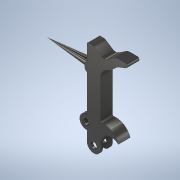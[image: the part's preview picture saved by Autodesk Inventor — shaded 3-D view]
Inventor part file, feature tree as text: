
AUTODESK INVENTOR PART (.ipt)
format: ipt  version: 2021 (Build 250183000, 183)  size: 390,144 bytes
history: native  units: in
note: dims shown in document units (in); Inventor stores cm internally (conversion verified against a paired STEP export)
features: extrude x8, sketch x8, plane x6, fillet x4, projected_geometry x2, revolve x1
ambient origin geometry x8: Origin, YZ Plane, XZ Plane, XY Plane, X Axis, Y Axis, Z Axis, Center Point
bodies: Solid1 (feature_tree)
feature tree (29):
  extrude  "Extrusion1"  Depth=0.9843in
  extrude  "Extrusion2"  Depth=0.0787in
  plane  "Work Plane1"
  extrude  "Extrusion3"  Depth=0.1575in TaperAngle=0.0deg
  plane  "Work Plane2"
  extrude  "Extrusion4"  Depth=0.0276in
  plane  "Work Plane3"
  fillet  "Fillet4"  Radius=0.22in
  plane  "Work Plane6"
  extrude  "Extrusion8"  Depth=0.0504in
  fillet  "Fillet8"  Radius=0.22in
  fillet  "Fillet9"  Radius=0.0157in
  plane  "Work Plane7"
  sketch  "Sketch10"  dims[d147=0.3937in d148=0.0in d149=0.1811in]
  extrude  "Extrusion9"  Depth=0.3937in
  extrude  "Extrusion10"  Depth=0.0157in
  extrude  "Extrusion11"  Depth=0.3937in
  plane  "Work Plane8"
  revolve  "Revolution1"  [1 undecoded]
  fillet  "Arredondamento11"  Radius=0.0004in
  sketch  "Sketch1"  dims[d0=1.4567in d1=0.9843in]
  sketch  "Sketch2"  dims[d2=0.1575in d3=0.0in d4=0.0787in]
  projected_geometry  "Projected Loop1"
  sketch  "Sketch3"  dims[d5=0.0787in d6=0.1575in d7=0.0in]
  sketch  "Sketch4"  dims[d8=0.0276in d9=0.0276in d10=0.22in d11=0.0in]
  sketch  "Sketch9"  dims[d12=0.0504in d13=0.0504in d14=0.22in d15=0.0in d31=0.0157in]
  sketch  "Sketch11"  dims[d157=0.0787in d158=0.0157in]
  projected_geometry  "Projected Loop4"
  sketch  "Sketch12"  dims[d160=0.0039in d161=8.2677in d163=0.0079in d164=0.3937in d166=0.3937in d168=0.0004in d169=0.0in d170=0.0004in d171=0.0in d173=0.0265in d174=0.0217in d175=0.0187in d176=0.0in d179=90.0deg d180=0.0394in]
note: 1 required parameter value undecoded (feature->parameter linkage not recoverable at this tier; creation-order binding heuristic only, values carry confidence <= 0.55)
